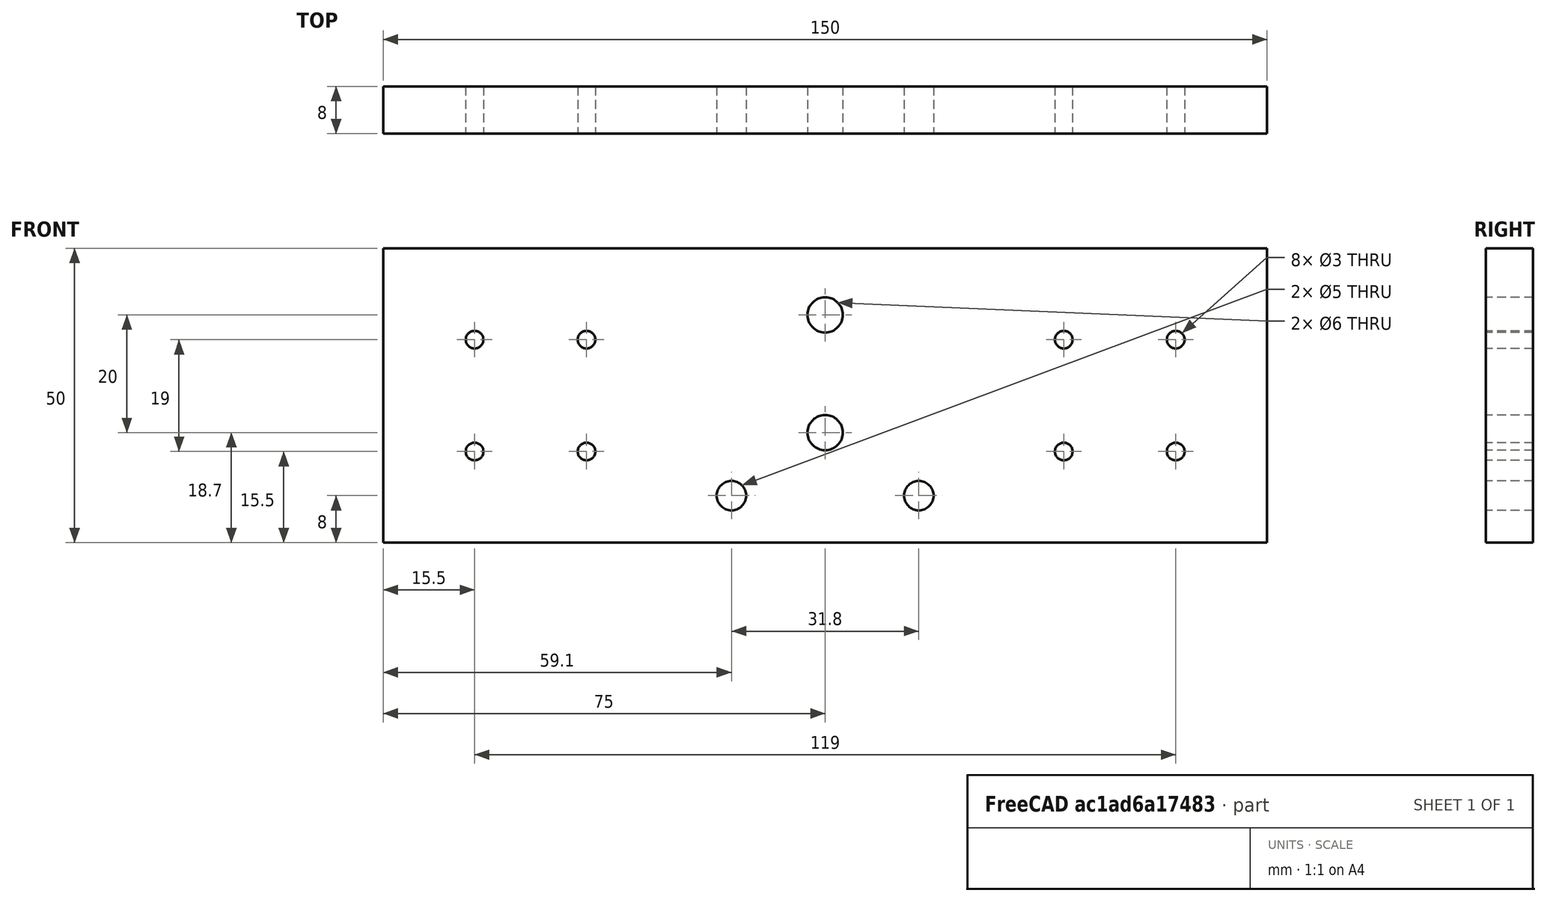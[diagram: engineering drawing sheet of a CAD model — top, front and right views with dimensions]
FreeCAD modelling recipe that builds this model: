
FCSTD DOCUMENT  (FreeCAD 0.14R3703 (Git))
Label: pletinaZ_taladros
License: CC-BY 3.0
LicenseURL: http://creativecommons.org/licenses/by/3.0/
objects: Part::Cylinder×12, Part::Cut×12, Part::Feature×2
note: 26 computed .brp shape members not serialized (recipe doc carries the construction recipe); baked Part::Feature solids carry a one-line shape summary decoded from their .brp

FEATURE [Part::Feature] Box  label="pletina_z_sin_agujeros"
  Placement = pos=(120,275,613) rot=(0,0,1;0rad)
  shape: bbox 150 x 8 x 50 mm, 6 faces (baked)
FEATURE [Part::Cylinder] Cylinder  label="Cilindro"
  Angle = 360
  Height = 30
  Placement = pos=(135.5,289.844,647.5) rot=(1,0,0;1.5708rad)
  Radius = 1.5
FEATURE [Part::Cylinder] Cylinder001  label="Cilindro001"
  Angle = 360
  Height = 30
  Placement = pos=(154.5,291.844,647.5) rot=(1,0,0;1.5708rad)
  Radius = 1.5
FEATURE [Part::Cylinder] Cylinder002  label="Cilindro002"
  Angle = 360
  Height = 30
  Placement = pos=(135.5,290.844,628.5) rot=(1,0,0;1.5708rad)
  Radius = 1.5
FEATURE [Part::Cylinder] Cylinder003  label="Cilindro003"
  Angle = 360
  Height = 30
  Placement = pos=(154.5,291.844,628.5) rot=(1,0,0;1.5708rad)
  Radius = 1.5
FEATURE [Part::Cylinder] Cylinder004  label="Cilindro004"
  Angle = 360
  Height = 30
  Placement = pos=(235.5,291.844,647.5) rot=(1,0,0;1.5708rad)
  Radius = 1.5
FEATURE [Part::Cylinder] Cylinder005  label="Cilindro005"
  Angle = 360
  Height = 30
  Placement = pos=(254.5,290.844,647.5) rot=(1,0,0;1.5708rad)
  Radius = 1.5
FEATURE [Part::Cylinder] Cylinder006  label="Cilindro006"
  Angle = 360
  Height = 30
  Placement = pos=(235.5,288.844,628.5) rot=(1,0,0;1.5708rad)
  Radius = 1.5
FEATURE [Part::Cylinder] Cylinder007  label="Cilindro007"
  Angle = 360
  Height = 30
  Placement = pos=(254.5,291.844,628.5) rot=(1,0,0;1.5708rad)
  Radius = 1.5
FEATURE [Part::Cylinder] Cylinder008  label="Cilindro008"
  Angle = 360
  Height = 30
  Placement = pos=(195,301,651.7) rot=(1,0,0;1.5708rad)
  Radius = 3
FEATURE [Part::Cylinder] Cylinder009  label="Cilindro009"
  Angle = 360
  Height = 30
  Placement = pos=(195,301,631.7) rot=(1,0,0;1.5708rad)
  Radius = 3
FEATURE [Part::Cylinder] Cylinder010  label="Cilindro010"
  Angle = 360
  Height = 30
  Placement = pos=(210.9,289,621) rot=(1,0,0;1.5708rad)
  Radius = 2.5
FEATURE [Part::Cylinder] Cylinder011  label="Cilindro011"
  Angle = 360
  Height = 30
  Placement = pos=(179.1,289,621) rot=(1,0,0;1.5708rad)
  Radius = 2.5
FEATURE [Part::Cut] Cut
  Base = -> Box
  Tool = -> Cylinder
FEATURE [Part::Cut] Cut001
  Base = -> Cut
  Tool = -> Cylinder011
FEATURE [Part::Cut] Cut002
  Base = -> Cut001
  Tool = -> Cylinder010
FEATURE [Part::Cut] Cut003
  Base = -> Cut002
  Tool = -> Cylinder009
FEATURE [Part::Cut] Cut004
  Base = -> Cut003
  Tool = -> Cylinder008
FEATURE [Part::Cut] Cut005
  Base = -> Cut004
  Tool = -> Cylinder007
FEATURE [Part::Cut] Cut006
  Base = -> Cut005
  Tool = -> Cylinder006
FEATURE [Part::Cut] Cut007
  Base = -> Cut006
  Tool = -> Cylinder005
FEATURE [Part::Cut] Cut008
  Base = -> Cut007
  Tool = -> Cylinder004
FEATURE [Part::Cut] Cut009
  Base = -> Cut008
  Tool = -> Cylinder003
FEATURE [Part::Cut] Cut010
  Base = -> Cut009
  Tool = -> Cylinder002
FEATURE [Part::Cut] Cut011
  Base = -> Cut010
  Tool = -> Cylinder001
FEATURE [Part::Feature] Cut012  label="pletina_Z_taladros"
  shape: bbox 150 x 8 x 50 mm, 18 faces (baked)
